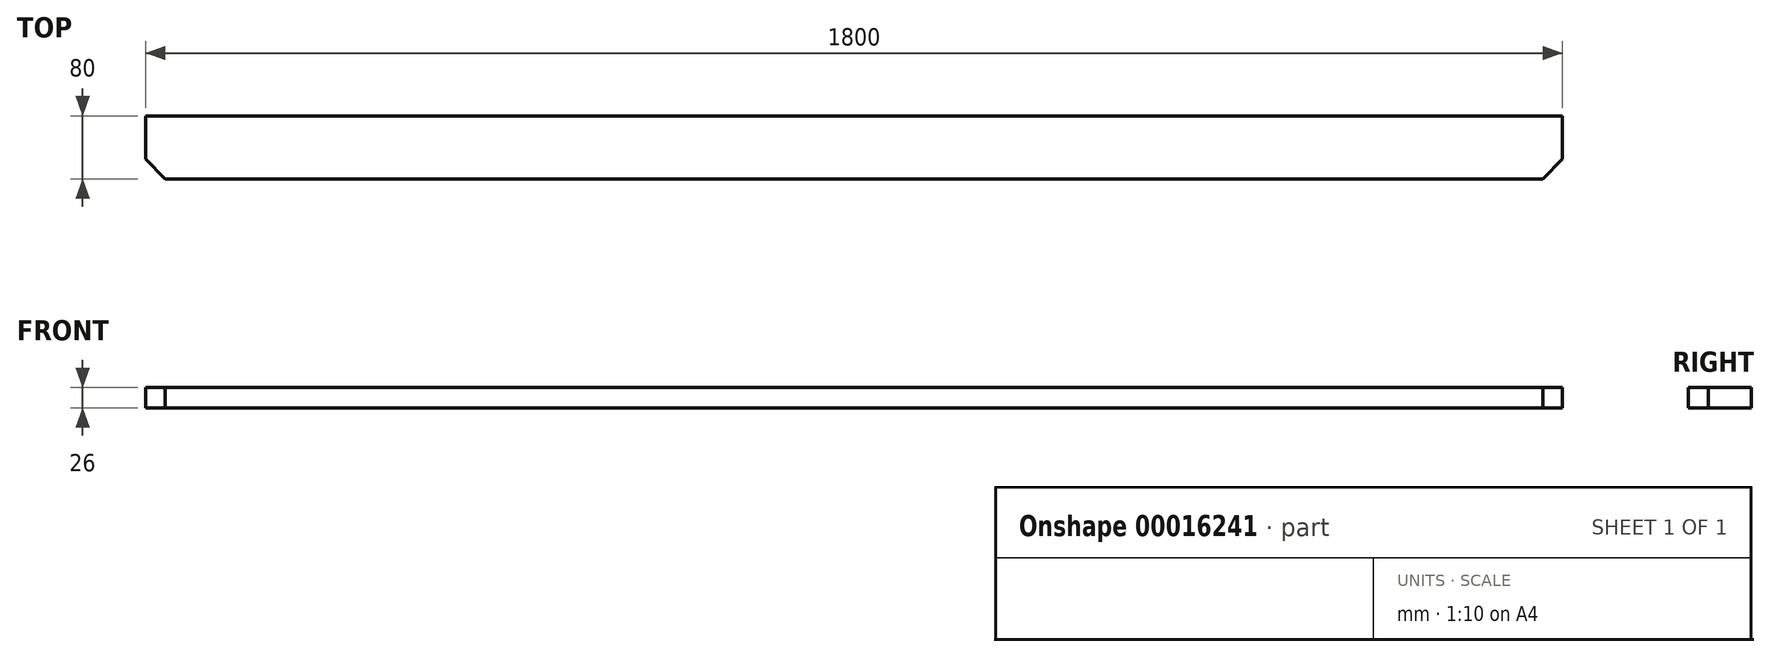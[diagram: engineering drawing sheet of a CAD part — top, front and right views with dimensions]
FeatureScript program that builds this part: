
annotation { "Feature Type Name" : "Feature", "Feature Type Description" : "" }
export const myFeature = defineFeature(function(context is Context, id is Id, definition is map)
    precondition{}
    {
        {
            var Q0;
            Q0=qCreatedBy(makeId("Top.planeOp"),FACE);
            var sketch = newSketch(context, id + "F0", { "sketchPlane" : qUnion([Q0])});
            skLineSegment(sketch, "E0.bottom", {"start": v(-127.08, 44.96) * mm, "end": v(1672.92, 44.96) * mm});
            skLineSegment(sketch, "E0.top", {"start": v(-127.08, -35.04) * mm, "end": v(1672.92, -35.04) * mm});
            skLineSegment(sketch, "E0.left", {"start": v(-127.08, 44.96) * mm, "end": v(-127.08, -35.04) * mm});
            skLineSegment(sketch, "E0.right", {"start": v(1672.92, 44.96) * mm, "end": v(1672.92, -35.04) * mm});
            skSolve(sketch);
        }
        {
            var Q0;
            Q0=makeQuery(id+"F0.imprint","IMPRINT",FACE,{"disambiguationData":[TD([[makeQuery(id+"F0.imprint","IMPRINT",EDGE,{"derivedFrom":sQuery(id+"F0.wireOp",EDGE,"E0.bottom")}),-1.0]])]});
            extrude(context, id + "F1", {"entities" : qUnion([Q0]), "depth" : 26 * mm});
        }
        {
            var Q0;
            Q0=makeQuery(id+"F1.opExtrude","CAP_FACE",FACE,{"disambiguationData":[OSD([sQuery(id+"F0.wireOp",EDGE,"E0.bottom"),sQuery(id+"F0.wireOp",EDGE,"E0.top"),sQuery(id+"F0.wireOp",EDGE,"E0.left"),sQuery(id+"F0.wireOp",EDGE,"E0.right")])],"isStart":false});
            var sketch = newSketch(context, id + "F2", { "sketchPlane" : qUnion([Q0])});
            skLineSegment(sketch, "E1", {"start": v(-127.08, -35.04) * mm, "end": v(-127.08, -10.04) * mm});
            skLineSegment(sketch, "E2", {"start": v(-127.08, -10.04) * mm, "end": v(-102.08, -35.04) * mm});
            skLineSegment(sketch, "E3", {"start": v(-102.08, -35.04) * mm, "end": v(-127.08, -35.04) * mm});
            skLineSegment(sketch, "E4", {"start": v(1672.92, -35.04) * mm, "end": v(1672.92, -10.04) * mm});
            skLineSegment(sketch, "E5", {"start": v(1672.92, -10.04) * mm, "end": v(1647.92, -35.04) * mm});
            skLineSegment(sketch, "E6", {"start": v(1647.92, -35.04) * mm, "end": v(1672.92, -35.04) * mm});
            skSolve(sketch);
        }
        {
            var Q0;
            Q0=makeQuery(id+"F2.imprint","IMPRINT",FACE,{"disambiguationData":[TD([[makeQuery(id+"F2.imprint","IMPRINT",EDGE,{"derivedFrom":sQuery(id+"F2.wireOp",EDGE,"E1")}),1.0]])]});
            var Q1;
            Q1=makeQuery(id+"F2.imprint","IMPRINT",FACE,{"disambiguationData":[TD([[makeQuery(id+"F2.imprint","IMPRINT",EDGE,{"derivedFrom":sQuery(id+"F2.wireOp",EDGE,"E4")}),-1.0]])]});
            extrude(context, id + "F3", {"entities" : qUnion([Q0, Q1]), "operationType" : NewBodyOperationType.REMOVE, "endBound" : BoundingType.THROUGH_ALL, "oppositeDirection" : true, "depth" : 25 * mm});
        }
    });
